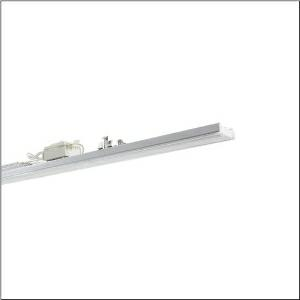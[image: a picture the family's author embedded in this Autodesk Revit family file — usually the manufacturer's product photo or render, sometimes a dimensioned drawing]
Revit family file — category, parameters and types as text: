
# Revit family: licross_11_recessed_ho_51tl12de47xm
name_source: partatom
category: Lighting Fixtures
units: mm (PartAtom-declared; Revit-internal decimal feet)

## family parameters
Cut with Voids When Loaded = No
Host = Face
Light Source = No
Part Type = Normal
Room Calculation Point = No
Round Connector Dimension = Use Diameter
Shared = No

## types (1)
- --- (1 x LED, 7020 lm, 40.2 W, 4000K)
    Apparent Load = 40 VA
    CIE Flux Codes = 66 91 98 100 100
    Color Rendering = 80
    Color Temperature = 4000K
    Default Elevation = 1800 mm
    Description = Licross 11 Recessed HO, luminaire insert, of sheet steel, coil coated, white, length: 750mm, width: 66mm, height: 67mm, LED rated luminous flux: 7.020lm, light colour: 840, SDCM (Standard Deviation of Colour Matching)MacAdam ≤ 2 SDCM (initial), control gear: DALI 2, with plug, 5-pole, with phase selection, mains connection: 220..240V, AC, 50/60Hz, rated input power: 40W, internal wiring halogen-free, primary optical cover: cover, of PMMA, light emission: direct distribution, primary light characteristic: symmetric, protection rating (complete): IP40, insulation class (complete): insulation class I (protective earthing), certification: CE, ENEC, VDE, UKCA, protection symbol: D if used in an environment without relevant dust loads with corresponding accessories, impact resistance: IK06, permissible ambient temperature for indoor applications: -25..+30°C, corresponds to IFS (International Featured Standards) requirements for safety and quality in the food industry, reducing of maximum allowable ambient temperature of 5°C with ceiling mounting, LABS conformity tested according to VDMA 24364:2018-05, The light source and the operating device comply with the requirements of the Ecodesign Regulation (EU) 2019/2020 and are replaceable in accordance with this regulation, packaging unit: 1 piece
    Height = 58 mm
    Lamp = 1 x LED
    Lamp Light Flux = 7020 lm
    Lamp Power = 40.2 W
    Lamp count = 1
    Length = 750 mm
    Luminous efficacy = 175 lm/W
    Manufacturer = Siteco
    ModVariant = No
    Model = 51TL12DE47XM
    Mounting Place = Ceiling
    Mounting Type = Pendant
    Number of Poles = 1
    OnlyDefault = Yes
    Power Factor = 1
    Product Name = Licross 11 Recessed HO
    Product group = luminaire insert | ceiling pendant
    ProductGroupID = 901
    Protection Class = Protection class I
    Protection Degree = IP 40
    RLX_Detail_Level = 1
    RLX_Emergency_Light_Flux = 0 lm
    RLX_Emergency_Type = 0
    RLX_Emergency_Type_DB = No
    RlxData = <blob elided: 29157 chars, md5=a31fe9cd>
    Socket = socket
    Standby Power = 0 W
    System Light Flux = 7020 lm
    System Power = 40 W
    Type Comments = factory setting: luminous flux: 100 % | dim-lin: 254 | 522 mA
    Type Image = l_1296930.jpg
    URL = http://relux.com
    VarID = @adj_101027
    Voltage = 0 V
    Weight = 0.00 kg
    Width = 66 mm

## geometry (parser evidence)
native form markers: Blend x4, Sweep x8
no freeform markers — native parametric forms only
